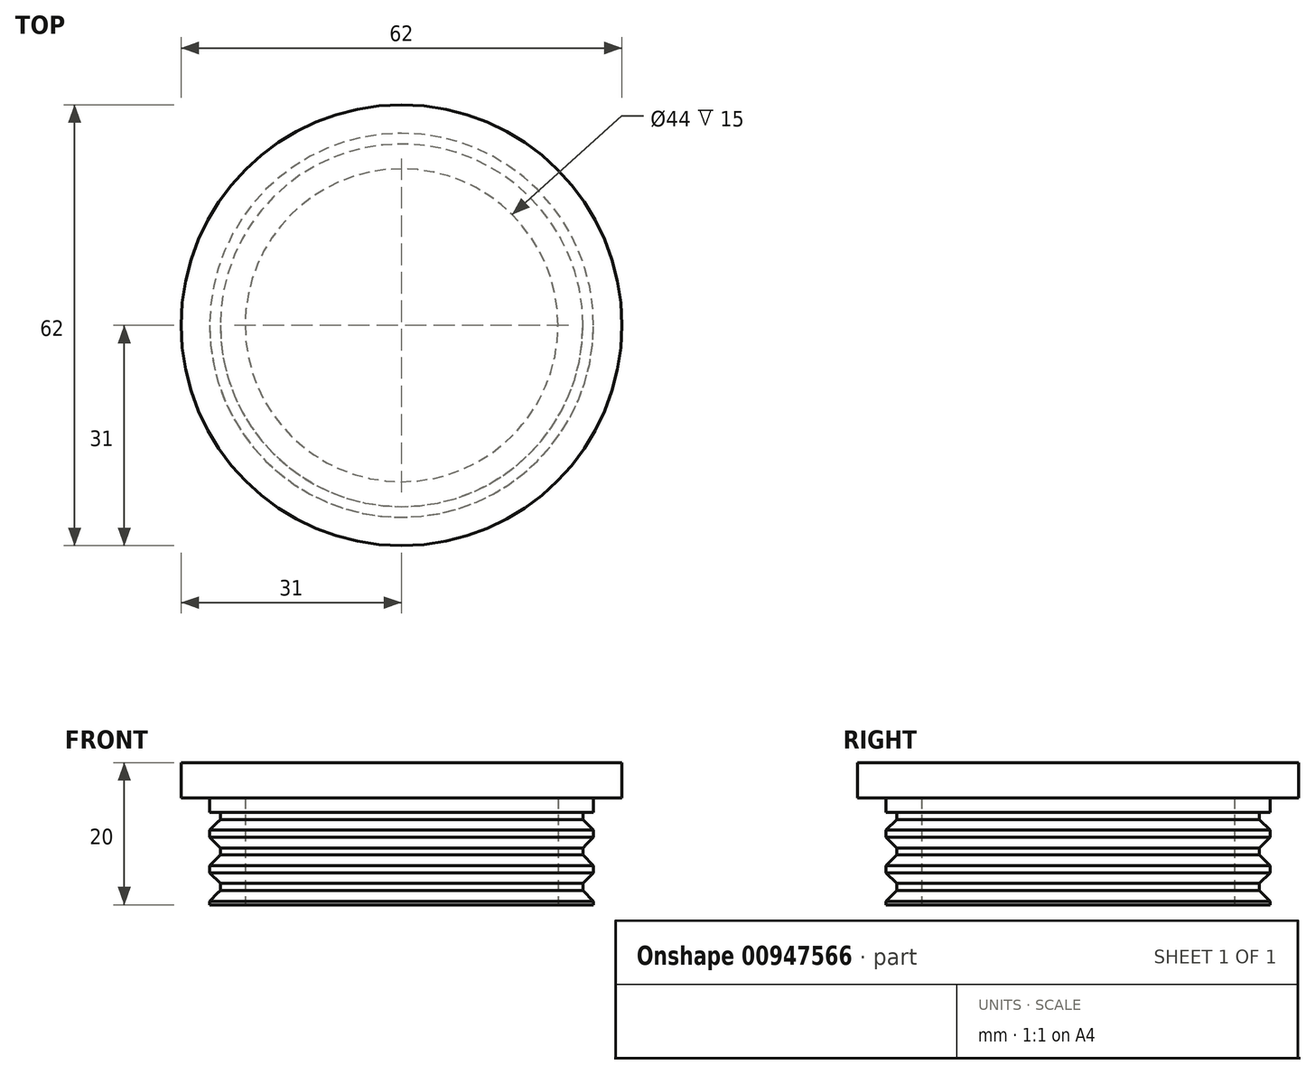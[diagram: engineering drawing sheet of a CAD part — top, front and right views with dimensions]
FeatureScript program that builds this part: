
annotation { "Feature Type Name" : "Feature", "Feature Type Description" : "" }
export const myFeature = defineFeature(function(context is Context, id is Id, definition is map)
    precondition{}
    {
        {
            var Q0;
            Q0=qCreatedBy(makeId("Top.planeOp"),FACE);
            var sketch = newSketch(context, id + "F0", { "sketchPlane" : qUnion([Q0])});
            skCircle(sketch, "E0", {"center": v(0, 0) * mm, "radius": 30 * mm});
            skCircle(sketch, "E1", {"center": v(0, 0) * mm, "radius": 27 * mm});
            skCircle(sketch, "E2", {"center": v(0, 0) * mm, "radius": 22 * mm});
            skSolve(sketch);
        }
        {
            var Q0;
            Q0=makeQuery(id+"F0.imprint","IMPRINT",FACE,{"disambiguationData":[TD([[makeQuery(id+"F0.imprint","IMPRINT",EDGE,{"derivedFrom":sQuery(id+"F0.wireOp",EDGE,"E1")}),1.0]])]});
            extrude(context, id + "F1", {"entities" : qUnion([Q0]), "depth" : 15 * mm, "offsetDistance" : 25 * mm});
        }
        {
            var Q0;
            Q0=makeQuery(id+"F1.opExtrude","CAP_FACE",FACE,{"disambiguationData":[OSD([sQuery(id+"F0.wireOp",EDGE,"E1"),sQuery(id+"F0.wireOp",EDGE,"E2")])],"isStart":false});
            var sketch = newSketch(context, id + "F2", { "sketchPlane" : qUnion([Q0])});
            skCircle(sketch, "E3", {"center": v(0, 0) * mm, "radius": 31 * mm});
            skSolve(sketch);
        }
        {
            var Q0;
            Q0=makeQuery(id+"F2.imprint","IMPRINT",FACE,{"disambiguationData":[TD([[makeQuery(id+"F2.imprint","IMPRINT",EDGE,{"derivedFrom":sQuery(id+"F2.wireOp",EDGE,"E3")}),1.0]])]});
            var Q1;
            Q1=makeQuery(id+"F2.imprint","IMPRINT",FACE,{"disambiguationData":[TD([[makeQuery(id+"F2.imprint","IMPRINT",EDGE,{"derivedFrom":makeQuery(id+"F1.opExtrude","CAP_EDGE",EDGE,{"disambiguationData":[OSD([sQuery(id+"F0.wireOp",EDGE,"E1")])],"isStart":false})}),1.0]])]});
            var Q2;
            Q2=makeQuery(id+"F2.imprint","IMPRINT",FACE,{"disambiguationData":[TD([[makeQuery(id+"F2.imprint","IMPRINT",EDGE,{"derivedFrom":makeQuery(id+"F1.opExtrude","CAP_EDGE",EDGE,{"disambiguationData":[OSD([sQuery(id+"F0.wireOp",EDGE,"E2")])],"isStart":false})}),1.0]])]});
            extrude(context, id + "F3", {"entities" : qUnion([Q0, Q1, Q2]), "depth" : 5 * mm, "offsetDistance" : 25 * mm});
        }
        {
            var Q0;
            Q0=qCreatedBy(makeId("Front.planeOp"),FACE);
            var sketch = newSketch(context, id + "F4", { "sketchPlane" : qUnion([Q0])});
            skLineSegment(sketch, "E4", {"start": v(0, 33.9) * mm, "end": v(0, -15.57) * mm, "construction": true});
            skLineSegment(sketch, "E5.bottom", {"start": v(-27, 2) * mm, "end": v(-25.5, 2) * mm});
            skLineSegment(sketch, "E5.top", {"start": v(-27, 3) * mm, "end": v(-25.5, 3) * mm});
            skLineSegment(sketch, "E5.left", {"start": v(-27, 2) * mm, "end": v(-27, 3) * mm});
            skLineSegment(sketch, "E5.right", {"start": v(-25.5, 2) * mm, "end": v(-25.5, 3) * mm});
            skLineSegment(sketch, "E6.bottom", {"start": v(-27, 7) * mm, "end": v(-25.5, 7) * mm});
            skLineSegment(sketch, "E6.top", {"start": v(-27, 8) * mm, "end": v(-25.5, 8) * mm});
            skLineSegment(sketch, "E6.left", {"start": v(-27, 7) * mm, "end": v(-27, 8) * mm});
            skLineSegment(sketch, "E6.right", {"start": v(-25.5, 7) * mm, "end": v(-25.5, 8) * mm});
            skLineSegment(sketch, "E7.bottom", {"start": v(-27, 12) * mm, "end": v(-25.5, 12) * mm});
            skLineSegment(sketch, "E7.top", {"start": v(-27, 13) * mm, "end": v(-25.5, 13) * mm});
            skLineSegment(sketch, "E7.left", {"start": v(-27, 12) * mm, "end": v(-27, 13) * mm});
            skLineSegment(sketch, "E7.right", {"start": v(-25.5, 12) * mm, "end": v(-25.5, 13) * mm});
            skLineSegment(sketch, "E8.bottom", {"start": v(-25.5, 12.5) * mm, "end": v(-25.5, 12.5) * mm});
            skLineSegment(sketch, "E8.top", {"start": v(-25.5, 14.36) * mm, "end": v(-25.5, 14.36) * mm});
            skLineSegment(sketch, "E9.bottom", {"start": v(0, 0) * mm, "end": v(27, 0) * mm});
            skLineSegment(sketch, "E9.top", {"start": v(0, 14.98) * mm, "end": v(27, 14.98) * mm});
            skLineSegment(sketch, "E9.left", {"start": v(0, 0) * mm, "end": v(0, 14.98) * mm});
            skLineSegment(sketch, "E9.right", {"start": v(27, 0) * mm, "end": v(27, 14.98) * mm});
            skLineSegment(sketch, "E10.bottom", {"start": v(0, 0) * mm, "end": v(-0.7, 0) * mm});
            skLineSegment(sketch, "E10.top", {"start": v(0, 0) * mm, "end": v(-0.7, 0) * mm});
            skLineSegment(sketch, "E10.left", {"start": v(0, 0) * mm, "end": v(0, 0) * mm});
            skLineSegment(sketch, "E10.right", {"start": v(-0.7, 0) * mm, "end": v(-0.7, 0) * mm});
            skLineSegment(sketch, "E11.bottom", {"start": v(0, 0) * mm, "end": v(-27, 0) * mm});
            skLineSegment(sketch, "E11.top", {"start": v(0, 14.93) * mm, "end": v(-27, 14.93) * mm});
            skLineSegment(sketch, "E11.left", {"start": v(0, 0) * mm, "end": v(0, 14.93) * mm});
            skLineSegment(sketch, "E11.right", {"start": v(-27, 0) * mm, "end": v(-27, 14.93) * mm});
            skSolve(sketch);
        }
        {
            var Q0;
            Q0=makeQuery(id+"F4.imprint","IMPRINT",FACE,{"disambiguationData":[TD([[makeQuery(id+"F4.imprint","IMPRINT",EDGE,{"derivedFrom":sQuery(id+"F4.wireOp",EDGE,"E5.bottom")}),1.0]])]});
            var Q1;
            Q1=makeQuery(id+"F4.imprint","IMPRINT",FACE,{"disambiguationData":[TD([[makeQuery(id+"F4.imprint","IMPRINT",EDGE,{"derivedFrom":sQuery(id+"F4.wireOp",EDGE,"E6.bottom")}),1.0]])]});
            var Q2;
            Q2=makeQuery(id+"F4.imprint","IMPRINT",FACE,{"disambiguationData":[TD([[makeQuery(id+"F4.imprint","IMPRINT",EDGE,{"derivedFrom":sQuery(id+"F4.wireOp",EDGE,"E7.bottom")}),1.0]])]});
            var Q3;
            Q3=sQuery(id+"F4.wireOp",EDGE,"E4");
            revolve(context, id + "F5", {"operationType" : NewBodyOperationType.REMOVE, "surfaceOperationType" : NewSurfaceOperationType.NEW, "entities" : qUnion([Q0, Q1, Q2]), "axis" : qUnion([Q3]), "revolveType" : RevolveType.FULL, "oppositeDirection" : true});
        }
        {
            var Q0;
            Q0=makeQuery(id+"F5.boolean.opBoolean","SPLIT",FACE,{"disambiguationData":[TD([makeQuery(id+"F5.opRevolve","SWEPT_FACE",FACE,{"disambiguationData":[OSD([sQuery(id+"F4.wireOp",EDGE,"E5.top")])]})])],"derivedFrom":makeQuery(id+"F1.opExtrude","SWEPT_FACE",FACE,{"disambiguationData":[OSD([sQuery(id+"F0.wireOp",EDGE,"E1")])]})});
            var Q1;
            Q1=makeQuery(id+"F5.boolean.opBoolean","COPY",EDGE,{"derivedFrom":makeQuery(id+"F5.opRevolve","SWEPT_EDGE",EDGE,{"disambiguationData":[OSD([sQuery(id+"F4.wireOp",EDGE,"E5.bottom"),sQuery(id+"F4.wireOp",EDGE,"E11.right")])]})});
            var Q2;
            Q2=makeQuery(id+"F5.boolean.opBoolean","SPLIT",FACE,{"disambiguationData":[TD([makeQuery(id+"F5.opRevolve","SWEPT_FACE",FACE,{"disambiguationData":[OSD([sQuery(id+"F4.wireOp",EDGE,"E6.top")])]})])],"derivedFrom":makeQuery(id+"F1.opExtrude","SWEPT_FACE",FACE,{"disambiguationData":[OSD([sQuery(id+"F0.wireOp",EDGE,"E1")])]})});
            var Q3;
            Q3=makeQuery(id+"F5.boolean.opBoolean","COPY",EDGE,{"derivedFrom":makeQuery(id+"F5.opRevolve","SWEPT_EDGE",EDGE,{"disambiguationData":[OSD([sQuery(id+"F4.wireOp",EDGE,"E7.top"),sQuery(id+"F4.wireOp",EDGE,"E11.right")])]})});
            chamfer(context, id + "F6", {"entities" : qUnion([Q0, Q1, Q2, Q3]), "chamferType" : ChamferType.OFFSET_ANGLE, "width" : 1.5 * mm, "oppositeDirection" : false, "angle" : 45 * degree, "tangentPropagation" : true});
        }
    });
